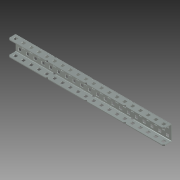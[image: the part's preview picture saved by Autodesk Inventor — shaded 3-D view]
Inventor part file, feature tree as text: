
AUTODESK INVENTOR PART (.ipt)
format: ipt  version: 2015 (Build 190159000, 159)  size: 1,350,144 bytes
history: native  units: in
note: dims shown in document units (in); Inventor stores cm internally (conversion verified against a paired STEP export)
features: other x109, extrude x99, sketch x12, pattern_linear x8, sheet_metal_op x5, mirror x3, plane x2, projected_geometry x2
ambient origin geometry x8: Origin, YZ Plane, XZ Plane, XY Plane, X Axis, Y Axis, Z Axis, Center Point
bodies: Solid1 (feature_tree)
feature tree (240):
  sheet_metal_op  "Face1"
  sheet_metal_op  "Flange1"
  sketch  "Sketch3"  dims[d2=0.032in]
  pattern_linear  "Rectangular Pattern1"  Spacing1=0.078in  [1 undecoded]
  pattern_linear  "Rectangular Pattern2"  Spacing1=0.182in  [1 undecoded]
  pattern_linear  "Rectangular Pattern3"  Spacing1=0.182in  [1 undecoded]
  pattern_linear  "Rectangular Pattern4"  Spacing1=0.159in  [1 undecoded]
  plane  "Work Plane1"
  sheet_metal_op  "Flange2"
  other  "Corner Chamfer1"
  pattern_linear  "Rectangular Pattern8"  Spacing1=0.02in  [1 undecoded]
  plane  "Work Plane2"
  mirror  "Mirror3"
  pattern_linear  "Rectangular Pattern9"  Spacing1=0.046in  [1 undecoded]
  mirror  "Mirror4"
  pattern_linear  "Rectangular Pattern10"  Spacing1=0.0in  [1 undecoded]
  pattern_linear  "Rectangular Pattern11"  Count1=20 Spacing1=0.5in
  mirror  "Mirror6"
  sketch  "Sketch1"  dims[d0=10.0in]
  other  "Plate1"
  sketch  "Sketch2"  dims[d1=0.546in]
  other  "Plate2"
  sheet_metal_op  "Bend1"
  projected_geometry  "Projected Loop1"
  projected_geometry  "Projected Loop2"
  sketch  "Sketch4"  dims[d3=0.046in]
  sketch  "Sketch5"  dims[d4=0.023in]
  sketch  "Sketch6"  dims[d5=0.092in]
  other  "Srf1"
  other  "Srf2"
  other  "Srf3"
  other  "Srf4"
  other  "Srf5"
  other  "Srf6"
  other  "Srf7"
  other  "Srf8"
  other  "Srf9"
  other  "Srf10"
  other  "Srf11"
  other  "Srf12"
  other  "Srf13"
  other  "Srf14"
  other  "Srf15"
  other  "Srf16"
  other  "Srf17"
  other  "Srf18"
  other  "Srf19"
  other  "Srf20"
  other  "Srf21"
  other  "Srf22"
  other  "Srf23"
  other  "Srf24"
  other  "Srf25"
  other  "Srf26"
  other  "Srf27"
  other  "Srf28"
  other  "Srf29"
  other  "Srf30"
  other  "Srf31"
  other  "Srf32"
  other  "Srf33"
  other  "Srf34"
  other  "Srf35"
  other  "Srf36"
  other  "Srf37"
  other  "Srf38"
  other  "Srf39"
  other  "Srf40"
  sketch  "Sketch7"  dims[d6=0.032in]
  other  "Srf401"
  other  "Srf402"
  other  "Srf403"
  other  "Srf404"
  other  "Srf405"
  other  "Srf406"
  other  "Srf407"
  other  "Srf408"
  other  "Srf409"
  other  "Srf410"
  other  "Srf411"
  other  "Srf412"
  other  "Srf413"
  other  "Srf414"
  other  "Srf415"
  other  "Srf416"
  other  "Srf417"
  other  "Srf418"
  other  "Srf419"
  other  "Work Axis1"
  sketch  "Sketch8"  dims[d7=0.954in d8=90.0deg d9=0.032in]
  sketch  "Sketch11"  dims[d10=0.184in]
  other  "Plate3"
  sheet_metal_op  "Bend2"
  sketch  "Sketch12"  dims[d11=0.046in]
  sketch  "Sketch13"  dims[d12=0.032in]
  sketch  "Sketch14"  dims[d13=0.032in d14=0.078in d15=0.182in d16=0.182in d18=0.159in d19=0.02in d20=0.046in d21=0.0in d22=7.874in d24=0.5in d25=0.7874in d27=0.5in d28=0.182in d29=0.182in d30=0.25in d31=0.25in d32=0.046in d33=0.0in d34=0.02in d35=7.4803in d37=0.5in d38=1.0in d39=0.0in d40=7.874in d42=0.5in d43=0.7874in d45=0.5in d46=1.0in d47=0.0in d48=7.4803in d50=0.5in d51=135.0deg d52=0.0in d53=0.0in d54=0.0in d55=0.0in d56=0.0in d57=0.0in d58=0.0in d59=0.0in d60=0.0in d61=0.0in d62=0.0in d63=0.0in d64=0.0in d65=0.0in d66=0.0in d67=0.0in d68=0.0in d69=0.0in d70=0.0in d71=0.0in d72=0.0in d73=0.0in d74=0.0in d75=0.0in d76=0.0in d77=0.0in d78=0.0in d79=0.0in d80=0.0in d81=0.0in d82=0.0in d83=0.0in d84=0.0in d85=0.0in d86=0.0in d87=0.0in d88=0.0in d89=0.0in d90=0.0in d91=0.0in d92=0.0in d93=0.0in d94=0.0in d95=0.0in d96=0.0in d97=0.0in d98=0.0in d99=0.0in d100=0.0in d101=0.0in d102=0.0in d103=0.0in d104=0.0in d105=0.0in d106=0.0in d107=0.0in d108=0.0in d109=0.0in d110=0.0in d111=0.0in d112=0.0in d113=0.0in d114=0.0in d115=0.0in d116=0.0in d117=0.0in d118=0.0in d119=0.0in d120=0.0in d121=0.0in d122=0.0in d123=0.0in d124=0.0in d125=0.0in d126=0.0in d127=0.0in d128=0.0in d129=0.0in d130=0.0in d131=0.0in d132=0.0in d133=0.0in d134=0.0in d135=0.0in d136=0.0in d137=0.0in d138=0.0in d139=0.0in d140=0.0in d141=0.0in d142=0.0in d143=0.0in d144=0.0in d145=0.0in d146=0.0in d147=0.0in d148=0.0in d149=0.0in d150=0.0in d151=0.0in d152=0.0in d153=0.0in d154=0.0in d155=0.0in d156=0.0in d157=0.0in d158=0.0in d159=0.0in d160=0.0in d161=0.0in d162=0.0in d163=0.0in d164=0.0in d165=0.0in d166=0.0in d167=0.0in d168=0.0in d169=0.0in d170=0.09in d171=0.25in d172=45.0deg d316=0.046in d317=0.023in d318=0.092in d319=0.032in d320=0.546in d321=90.0deg d322=0.032in d323=0.184in d324=0.046in d325=0.032in d326=0.581in d330=0.078in d331=0.039in d333=0.046in d334=0.6508in d335=0.046in d336=0.0in d337=1.1811in d339=2.5in d340=90.0deg d341=0.16in d342=0.046in d343=0.0in d344=1.1811in d346=2.5in d347=0.206in d348=0.182in d349=0.02in d350=0.159in d351=0.046in d352=0.0in d353=7.874in d355=0.5in d356=1.0in d357=0.0in d358=7.874in d360=0.5in d361=0.0in d362=0.0in d363=0.0in d364=0.0in d365=0.0in d366=0.0in d367=0.0in d368=0.0in d369=0.0in d370=0.0in d371=0.0in d372=0.0in d373=0.0in d374=0.0in d375=0.0in d376=0.0in d377=0.0in d378=0.0in d379=0.0in d380=0.0in d381=0.0in d382=0.0in d383=0.0in d384=0.0in d385=0.0in d386=0.0in d387=0.0in d388=0.0in d389=0.0in d390=0.0in d391=0.0in d392=0.0in d393=0.0in d394=0.0in d395=0.0in d396=0.0in d397=0.0in d398=0.0in d399=0.0in d400=0.0in d401=0.0in d402=0.0in d403=0.0in d404=0.0in d405=0.0in d406=0.0in d407=0.0in d408=0.0in d409=0.0in d410=0.0in d411=0.0in d412=0.0in d413=0.0in d414=0.0in d415=0.0in d416=0.0in d417=0.0in d418=0.0in d419=0.0in d420=0.0in d421=0.0in d422=0.0in d423=0.0in d424=0.0in d425=0.0in d426=0.0in d427=0.0in d428=0.0in d429=0.0in d430=0.0in d431=0.0in d432=0.0in d433=0.0in d434=0.0in d435=0.0in d436=0.0in d437=0.0in d438=0.0in d439=0.0in d440=0.0in]
  other  "Srf479"
  other  "Srf480"
  other  "Srf481"
  other  "Srf482"
  other  "Srf483"
  other  "Srf484"
  other  "Srf485"
  other  "Srf486"
  other  "Srf487"
  other  "Srf488"
  other  "Srf489"
  other  "Srf490"
  other  "Srf491"
  other  "Srf492"
  other  "Srf493"
  other  "Srf494"
  other  "Srf495"
  other  "Srf496"
  other  "Srf497"
  other  "Srf498"
  other  "Srf519"
  other  "Srf520"
  other  "Srf521"
  other  "Srf522"
  other  "Srf523"
  other  "Srf524"
  other  "Srf525"
  other  "Srf526"
  other  "Srf527"
  other  "Srf528"
  other  "Srf529"
  other  "Srf530"
  other  "Srf531"
  other  "Srf532"
  other  "Srf533"
  other  "Srf534"
  other  "Srf535"
  other  "Srf536"
  other  "Srf537"
  other  "Srf538"
  other  "Cut1"
  other  "Cut2"
  extrude  "ExtrusionSrf1"  Depth=0.5in
  extrude  "ExtrusionSrf401"  Depth=0.182in
  other  "Cut6"
  other  "Cut7"
  other  "Cut8"
  extrude  "ExtrusionSrf479"  Depth=0.182in
  extrude  "ExtrusionSrf2"  Depth=0.5in
  extrude  "ExtrusionSrf3"  Depth=0.5in
  extrude  "ExtrusionSrf4"  Depth=0.046in
  extrude  "ExtrusionSrf5"  TaperAngle=0.0deg  [1 undecoded]
  extrude  "ExtrusionSrf6"  Depth=0.02in
  extrude  "ExtrusionSrf7"  Depth=0.5in
  extrude  "ExtrusionSrf8"  Depth=1.0in TaperAngle=0.0deg
  extrude  "ExtrusionSrf9"  Depth=0.5in
  extrude  "ExtrusionSrf10"  Depth=1.0in TaperAngle=0.0deg
  extrude  "ExtrusionSrf11"  Depth=0.5in
  extrude  "ExtrusionSrf12"  Depth=0.046in
  extrude  "ExtrusionSrf13"  Depth=0.5in
  extrude  "ExtrusionSrf14"  Depth=0.5in
  extrude  "ExtrusionSrf15"  Depth=0.5in
  extrude  "ExtrusionSrf16"  Depth=0.5in TaperAngle=90.0deg
  extrude  "ExtrusionSrf17"  Depth=0.5in
  extrude  "ExtrusionSrf18"  Depth=0.046in
  extrude  "ExtrusionSrf19"  Depth=0.5in
  extrude  "ExtrusionSrf20"  Depth=0.5in
  extrude  "ExtrusionSrf21"  Depth=0.5in
  extrude  "ExtrusionSrf22"  Depth=0.5in
  extrude  "ExtrusionSrf23"  Depth=0.046in
  extrude  "ExtrusionSrf24"  Depth=0.5in
  extrude  "ExtrusionSrf25"  Depth=0.046in
  extrude  "ExtrusionSrf26"  TaperAngle=0.0deg  [1 undecoded]
  extrude  "ExtrusionSrf27"  Depth=2.5in
  extrude  "ExtrusionSrf28"  TaperAngle=90.0deg  [1 undecoded]
  extrude  "ExtrusionSrf29"  Depth=0.5in
  extrude  "ExtrusionSrf30"  Depth=0.046in
  extrude  "ExtrusionSrf31"  TaperAngle=0.0deg  [1 undecoded]
  extrude  "ExtrusionSrf32"  Depth=2.5in
  extrude  "ExtrusionSrf33"  Depth=0.5in
  extrude  "ExtrusionSrf34"  Depth=0.182in
  extrude  "ExtrusionSrf35"  Depth=0.02in
  extrude  "ExtrusionSrf36"  Depth=0.159in
  extrude  "ExtrusionSrf37"  Depth=0.046in
  extrude  "ExtrusionSrf38"  TaperAngle=0.0deg  [1 undecoded]
  extrude  "ExtrusionSrf39"  Depth=0.5in
  extrude  "ExtrusionSrf40"  Depth=1.0in TaperAngle=0.0deg
  extrude  "ExtrusionSrf402"  Depth=0.5in
  extrude  "ExtrusionSrf403"  [1 undecoded]
  extrude  "ExtrusionSrf404"  [1 undecoded]
  extrude  "ExtrusionSrf405"  [1 undecoded]
  extrude  "ExtrusionSrf406"  [1 undecoded]
  extrude  "ExtrusionSrf407"  [1 undecoded]
  extrude  "ExtrusionSrf408"  [1 undecoded]
  extrude  "ExtrusionSrf409"  [1 undecoded]
  extrude  "ExtrusionSrf410"  [1 undecoded]
  extrude  "ExtrusionSrf411"  [1 undecoded]
  extrude  "ExtrusionSrf412"  [1 undecoded]
  extrude  "ExtrusionSrf413"  [1 undecoded]
  extrude  "ExtrusionSrf414"  [1 undecoded]
  extrude  "ExtrusionSrf415"  [1 undecoded]
  extrude  "ExtrusionSrf416"  [1 undecoded]
  extrude  "ExtrusionSrf417"  [1 undecoded]
  extrude  "ExtrusionSrf418"  [1 undecoded]
  extrude  "ExtrusionSrf419"  [1 undecoded]
  extrude  "ExtrusionSrf480"  [1 undecoded]
  extrude  "ExtrusionSrf481"  [1 undecoded]
  extrude  "ExtrusionSrf482"  [1 undecoded]
  extrude  "ExtrusionSrf483"  [1 undecoded]
  extrude  "ExtrusionSrf484"  [1 undecoded]
  extrude  "ExtrusionSrf485"  [1 undecoded]
  extrude  "ExtrusionSrf486"  [1 undecoded]
  extrude  "ExtrusionSrf487"  [1 undecoded]
  extrude  "ExtrusionSrf488"  [1 undecoded]
  extrude  "ExtrusionSrf489"  [1 undecoded]
  extrude  "ExtrusionSrf490"  [1 undecoded]
  extrude  "ExtrusionSrf491"  [1 undecoded]
  extrude  "ExtrusionSrf492"  [1 undecoded]
  extrude  "ExtrusionSrf493"  [1 undecoded]
  extrude  "ExtrusionSrf494"  [1 undecoded]
  extrude  "ExtrusionSrf495"  [1 undecoded]
  extrude  "ExtrusionSrf496"  [1 undecoded]
  extrude  "ExtrusionSrf497"  [1 undecoded]
  extrude  "ExtrusionSrf498"  [1 undecoded]
  extrude  "ExtrusionSrf519"  [1 undecoded]
  extrude  "ExtrusionSrf520"  [1 undecoded]
  extrude  "ExtrusionSrf521"  [1 undecoded]
  extrude  "ExtrusionSrf522"  [1 undecoded]
  extrude  "ExtrusionSrf523"  [1 undecoded]
  extrude  "ExtrusionSrf524"  [1 undecoded]
  extrude  "ExtrusionSrf525"  [1 undecoded]
  extrude  "ExtrusionSrf526"  [1 undecoded]
  extrude  "ExtrusionSrf527"  [1 undecoded]
  extrude  "ExtrusionSrf528"  [1 undecoded]
  extrude  "ExtrusionSrf529"  [1 undecoded]
  extrude  "ExtrusionSrf530"  [1 undecoded]
  extrude  "ExtrusionSrf531"  [1 undecoded]
  extrude  "ExtrusionSrf532"  [1 undecoded]
  extrude  "ExtrusionSrf533"  [1 undecoded]
  extrude  "ExtrusionSrf534"  [1 undecoded]
  extrude  "ExtrusionSrf535"  [1 undecoded]
  extrude  "ExtrusionSrf536"  [1 undecoded]
  extrude  "ExtrusionSrf537"  [1 undecoded]
  extrude  "ExtrusionSrf538"  [1 undecoded]
note: 68 required parameter values undecoded (feature->parameter linkage not recoverable at this tier; creation-order binding heuristic only, values carry confidence <= 0.55)
